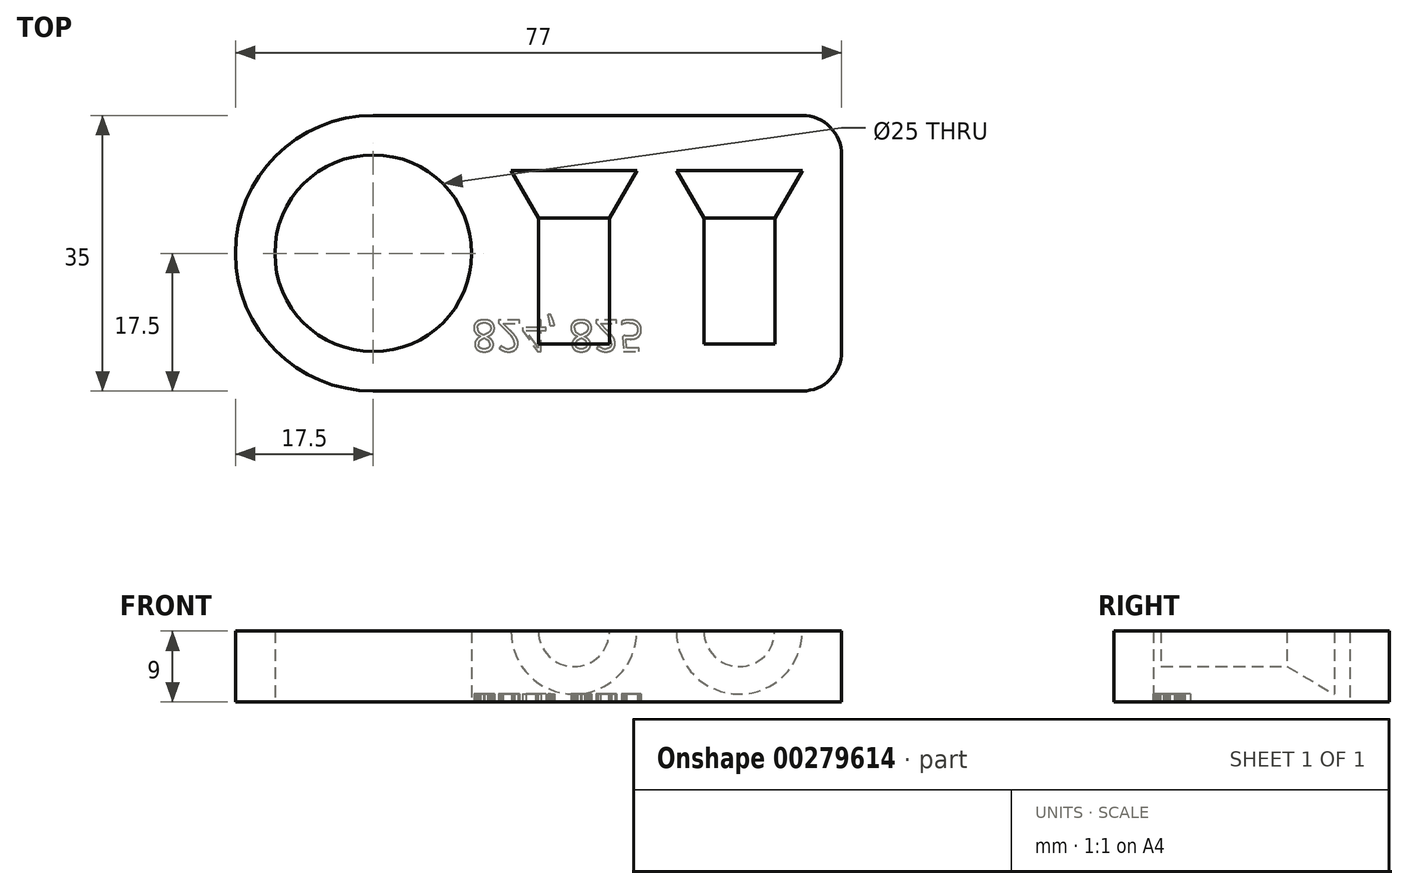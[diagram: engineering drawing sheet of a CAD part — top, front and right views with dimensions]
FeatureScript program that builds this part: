
annotation { "Feature Type Name" : "Feature", "Feature Type Description" : "" }
export const myFeature = defineFeature(function(context is Context, id is Id, definition is map)
    precondition{}
    {
        {
            var Q0;
            Q0=qCreatedBy(makeId("Top.planeOp"),FACE);
            var sketch = newSketch(context, id + "F0", { "sketchPlane" : qUnion([Q0])});
            skLineSegment(sketch, "E0.bottom", {"start": v(17.5, 0) * mm, "end": v(72, 0) * mm});
            skLineSegment(sketch, "E0.top", {"start": v(17.5, 35) * mm, "end": v(72, 35) * mm});
            skLineSegment(sketch, "E0.left", {"start": v(0, 17.5) * mm, "end": v(0, 17.5) * mm});
            skLineSegment(sketch, "E0.right", {"start": v(77, 5) * mm, "end": v(77, 30) * mm});
            skLineSegment(sketch, "E1.bottom", {"start": v(0, 0) * mm, "end": v(17.5, 0) * mm, "construction": true});
            skLineSegment(sketch, "E1.top", {"start": v(0, 17.5) * mm, "end": v(17.5, 17.5) * mm, "construction": true});
            skLineSegment(sketch, "E1.left", {"start": v(0, 0) * mm, "end": v(0, 17.5) * mm, "construction": true});
            skLineSegment(sketch, "E1.right", {"start": v(17.5, 0) * mm, "end": v(17.5, 17.5) * mm, "construction": true});
            skCircle(sketch, "E2", {"center": v(17.5, 17.5) * mm, "radius": 12.5 * mm});
            skPoint(sketch, "E3.visualSharp", {"position": v(0, 0) * mm});
            skArc(sketch, "E3.filletArc", {"start": v(0, 17.5) * mm, "mid": v(5.13, 5.13) * mm, "end": v(17.5, 0) * mm});
            skPoint(sketch, "E4.visualSharp", {"position": v(0, 35) * mm});
            skArc(sketch, "E4.filletArc", {"start": v(17.5, 35) * mm, "mid": v(5.13, 29.87) * mm, "end": v(0, 17.5) * mm});
            skPoint(sketch, "E5.visualSharp", {"position": v(77, 35) * mm});
            skArc(sketch, "E5.filletArc", {"start": v(77, 30) * mm, "mid": v(75.54, 33.54) * mm, "end": v(72, 35) * mm});
            skPoint(sketch, "E6.visualSharp", {"position": v(77, 0) * mm});
            skArc(sketch, "E6.filletArc", {"start": v(72, 0) * mm, "mid": v(75.54, 1.46) * mm, "end": v(77, 5) * mm});
            skSolve(sketch);
        }
        {
            var Q0;
            Q0=makeQuery(id+"F0.imprint","IMPRINT",FACE,{"disambiguationData":[TD([[makeQuery(id+"F0.imprint","IMPRINT",EDGE,{"derivedFrom":sQuery(id+"F0.wireOp",EDGE,"E0.bottom")}),1.0]])]});
            extrude(context, id + "F1", {"entities" : qUnion([Q0]), "depth" : 9 * mm});
        }
        {
            var Q0;
            Q0=makeQuery(id+"F1.opExtrude","CAP_FACE",FACE,{"disambiguationData":[OSD([sQuery(id+"F0.wireOp",EDGE,"E0.bottom"),sQuery(id+"F0.wireOp",EDGE,"E0.top"),sQuery(id+"F0.wireOp",EDGE,"E0.right"),sQuery(id+"F0.wireOp",EDGE,"E2"),sQuery(id+"F0.wireOp",EDGE,"E3.filletArc"),sQuery(id+"F0.wireOp",EDGE,"E4.filletArc"),sQuery(id+"F0.wireOp",EDGE,"E5.filletArc"),sQuery(id+"F0.wireOp",EDGE,"E6.filletArc")])],"isStart":false});
            var sketch = newSketch(context, id + "F2", { "sketchPlane" : qUnion([Q0])});
            skLineSegment(sketch, "E7.bottom", {"start": v(0, 0) * mm, "end": v(43, 0) * mm, "construction": true});
            skLineSegment(sketch, "E7.top", {"start": v(0, 6) * mm, "end": v(43, 6) * mm, "construction": true});
            skLineSegment(sketch, "E7.left", {"start": v(0, 0) * mm, "end": v(0, 6) * mm, "construction": true});
            skLineSegment(sketch, "E7.right", {"start": v(43, 0) * mm, "end": v(43, 6) * mm, "construction": true});
            skLineSegment(sketch, "E8", {"start": v(43, 6) * mm, "end": v(64, 6) * mm, "construction": true});
            skLineSegment(sketch, "E9", {"start": v(43, 6) * mm, "end": v(43, 28) * mm});
            skLineSegment(sketch, "E10", {"start": v(43, 28) * mm, "end": v(51, 28) * mm});
            skLineSegment(sketch, "E11", {"start": v(43, 6) * mm, "end": v(47.5, 6) * mm});
            skLineSegment(sketch, "E12", {"start": v(47.5, 6) * mm, "end": v(47.5, 22) * mm});
            skLineSegment(sketch, "E13", {"start": v(47.5, 22) * mm, "end": v(51, 28) * mm});
            skLineSegment(sketch, "E14", {"start": v(64, 6) * mm, "end": v(64, 28) * mm});
            skLineSegment(sketch, "E15", {"start": v(64, 28) * mm, "end": v(72, 28) * mm});
            skLineSegment(sketch, "E16", {"start": v(64, 6) * mm, "end": v(68.5, 6) * mm});
            skLineSegment(sketch, "E17", {"start": v(68.5, 6) * mm, "end": v(68.5, 22) * mm});
            skLineSegment(sketch, "E18", {"start": v(68.5, 22) * mm, "end": v(72, 28) * mm});
            skSolve(sketch);
        }
        {
            var Q0;
            Q0=makeQuery(id+"F2.imprint","IMPRINT",FACE,{"disambiguationData":[TD([[makeQuery(id+"F2.imprint","IMPRINT",EDGE,{"derivedFrom":sQuery(id+"F2.wireOp",EDGE,"E9")}),-1.0]])]});
            var Q1;
            Q1=sQuery(id+"F2.wireOp",EDGE,"E9");
            revolve(context, id + "F3", {"operationType" : NewBodyOperationType.REMOVE, "entities" : qUnion([Q0]), "axis" : qUnion([Q1]), "revolveType" : RevolveType.FULL, "oppositeDirection" : true});
        }
        {
            var Q0;
            Q0=makeQuery(id+"F2.imprint","IMPRINT",FACE,{"disambiguationData":[TD([[makeQuery(id+"F2.imprint","IMPRINT",EDGE,{"derivedFrom":sQuery(id+"F2.wireOp",EDGE,"E14")}),-1.0]])]});
            var Q1;
            Q1=sQuery(id+"F2.wireOp",EDGE,"E14");
            revolve(context, id + "F4", {"operationType" : NewBodyOperationType.REMOVE, "entities" : qUnion([Q0]), "axis" : qUnion([Q1]), "revolveType" : RevolveType.FULL, "oppositeDirection" : true});
        }
        {
            var Q0;
            Q0=makeQuery(id+"F1.opExtrude","CAP_FACE",FACE,{"disambiguationData":[OSD([sQuery(id+"F0.wireOp",EDGE,"E0.bottom"),sQuery(id+"F0.wireOp",EDGE,"E0.top"),sQuery(id+"F0.wireOp",EDGE,"E0.right"),sQuery(id+"F0.wireOp",EDGE,"E2"),sQuery(id+"F0.wireOp",EDGE,"E3.filletArc"),sQuery(id+"F0.wireOp",EDGE,"E4.filletArc"),sQuery(id+"F0.wireOp",EDGE,"E5.filletArc"),sQuery(id+"F0.wireOp",EDGE,"E6.filletArc")])],"isStart":true});
            var sketch = newSketch(context, id + "F5", { "sketchPlane" : qUnion([Q0])});
            skLineSegment(sketch, "E19.bottom", {"start": v(0, 0) * mm, "end": v(30, 0) * mm, "construction": true});
            skLineSegment(sketch, "E19.top", {"start": v(0, -5) * mm, "end": v(30, -5) * mm, "construction": true});
            skLineSegment(sketch, "E19.left", {"start": v(0, 0) * mm, "end": v(0, -5) * mm, "construction": true});
            skLineSegment(sketch, "E19.right", {"start": v(30, 0) * mm, "end": v(30, -5) * mm, "construction": true});
            skText(sketch, "E20", { "text": "824, 825", "fontName": "OpenSans-Regular.ttf"});
            const initialGuessF5  = {"E20": [0.03, -0.009, 1, 0, 0.004]};
            skSetInitialGuess(sketch, initialGuessF5);
            skSolve(sketch);
        }
        {
            var Q0;
            Q0 = qSketchRegion(id + "F5", true);
            extrude(context, id + "F6", {"entities" : qUnion([Q0]), "operationType" : NewBodyOperationType.REMOVE, "oppositeDirection" : true, "depth" : 1 * mm});
        }
    });
